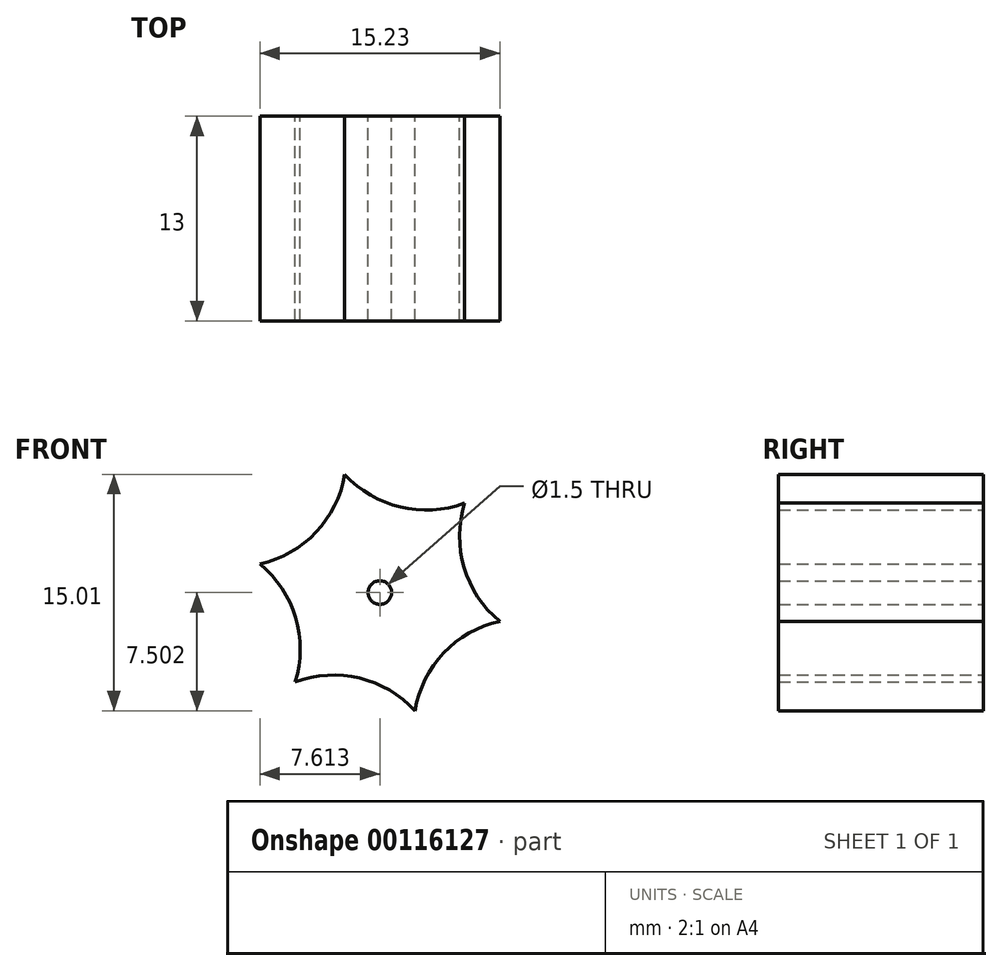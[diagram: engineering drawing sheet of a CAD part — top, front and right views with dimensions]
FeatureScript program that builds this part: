
annotation { "Feature Type Name" : "Feature", "Feature Type Description" : "" }
export const myFeature = defineFeature(function(context is Context, id is Id, definition is map)
    precondition{}
    {
        {
            var Q0;
            Q0=qCreatedBy(makeId("Front.planeOp"),FACE);
            var sketch = newSketch(context, id + "F0", { "sketchPlane" : qUnion([Q0])});
            skPoint(sketch, "E0.0.midPoint", {"position": v(-38.72, 24.9) * mm});
            skCircle(sketch, "E1", {"center": v(-43.65, 29.57) * mm, "radius": 0.75 * mm});
            skArc(sketch, "E2", {"start": v(-51.26, 31.4) * mm, "mid": v(-47.7, 33.41) * mm, "end": v(-45.88, 37.08) * mm});
            skArc(sketch, "E3", {"start": v(-45.88, 37.08) * mm, "mid": v(-42.35, 35) * mm, "end": v(-38.26, 35.26) * mm});
            skArc(sketch, "E4", {"start": v(-38.26, 35.26) * mm, "mid": v(-38.3, 31.16) * mm, "end": v(-36.03, 27.75) * mm});
            skArc(sketch, "E5", {"start": v(-36.03, 27.75) * mm, "mid": v(-39.6, 25.73) * mm, "end": v(-41.42, 22.07) * mm});
            skArc(sketch, "E6", {"start": v(-41.42, 22.07) * mm, "mid": v(-44.95, 24.14) * mm, "end": v(-49.03, 23.89) * mm});
            skArc(sketch, "E7", {"start": v(-49.03, 23.89) * mm, "mid": v(-49, 27.98) * mm, "end": v(-51.26, 31.4) * mm});
            skSolve(sketch);
        }
        {
            var Q0;
            Q0=makeQuery(id+"F0.imprint","IMPRINT",FACE,{"disambiguationData":[TD([[makeQuery(id+"F0.imprint","IMPRINT",EDGE,{"derivedFrom":sQuery(id+"F0.wireOp",EDGE,"E1")}),-1.0]])]});
            extrude(context, id + "F1", {"entities" : qUnion([Q0]), "depth" : 13 * mm});
        }
    });
